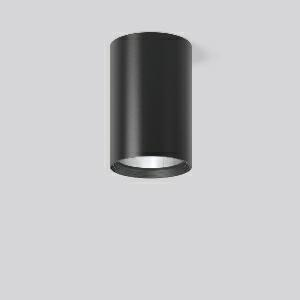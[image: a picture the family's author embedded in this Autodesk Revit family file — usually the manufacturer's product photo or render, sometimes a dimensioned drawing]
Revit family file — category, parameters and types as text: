
# Revit family: heledon_maxi_a_931231_003_9655
name_source: partatom
category: Lighting Fixtures
units: mm (PartAtom-declared; Revit-internal decimal feet)

## family parameters
Cut with Voids When Loaded = No
Host = Face
Light Source = No
Part Type = Normal
Room Calculation Point = No
Round Connector Dimension = Use Diameter
Shared = No

## types (1)
- HELEDON maxi A (1 x LED Modul 932 fresh meat, 2150 lm, 3200)
    Apparent Load = 33 VA
    Approval mark = CE
    CIE Flux Codes = 100 100 100 100 100
    Color Rendering = 90
    Color Temperature = 3200
    Default Elevation = 1800 mm
    Description = Series: HELEDON maxi
Cylindrical surface-mounted downlight. Housing: die-cast aluminium, powder-coated. Internal ceiling frame polycarbonate with bayonet mounting. Black plastic ring and recessed LED to prevent glare from the side. Optical assembly with reflector made of MIRO-Silver with 98% total light reflection for outstanding efficiency - can be changed without tools. Special LED for illumination of meat included. Suitable for Ceiling mounting. Easy installation with a separate ceiling frame with bayonet mounting and plug connection. Driver integrated. Connected via plug-in connector. High quality converter without flickering and stroboscopic effect. The following accessories can be mounted without use of tools: interchangeable lenses, decorative glasses, honeycomb louvre, clear and frosted diffusers, white interchangeable plastic ring. 
Colour: deep black, matt (RAL 9005)
Diameter: 123 mm
Height: 183 mm
Lamp: LED
Socket: without socket
Colour temperature: fresh meat
System power: 33 W
Rated luminous flux: 2150 lm
Luminous efficiency: 65 lm/W
Control gear: Regulated power supply
Protection class: I
Type of protection: IP 20
    Height = 183 mm
    Lamp = 1 x LED Modul 932 fresh meat
    Lamp Light Flux = 2150 lm
    Lamp count = 1
    Length = 123 mm
    Lifetime = 50000 h
    Luminous efficacy = 65 lm/W
    Manufacturer = RZB
    ModVariant = No
    Model = 931231.003
    Mounting Place = Ceiling
    Mounting Type = Surface mounted
    Number of Poles = 1
    OnlyDefault = Yes
    Power Factor = 1
    Product Name = HELEDON maxi A
    Product group = Surface mounted downlights
    ProductGroupID = 302
    Protection Class = Protection class I
    Protection Degree = IP 20
    RLX_Detail_Level = 1
    RLX_Emergency_Light_Flux = 0 lm
    RLX_Emergency_Type = 0
    RLX_Emergency_Type_DB = No
    RlxData = <blob elided: 97265 chars, md5=ce9cba43>
    Socket = socket
    Standby Power = 0 W
    System Light Flux = 2150 lm
    System Power = 33 W
    Type Comments = Product without accessories
    Type Image = 931192.003.jpg
    URL = http://relux.com
    VarID = ---
    Voltage = 230 V
    Voltage Range = 220-240 V
    Weight = 0.00 kg
    Width = 0 mm  [stored 0 ft]

note: [stored X ft] marks values corroborated as IEEE doubles in the binary element streams (Revit-internal decimal feet)

## geometry (parser evidence)
native form markers: Blend x4, Sweep x11
no freeform markers — native parametric forms only
